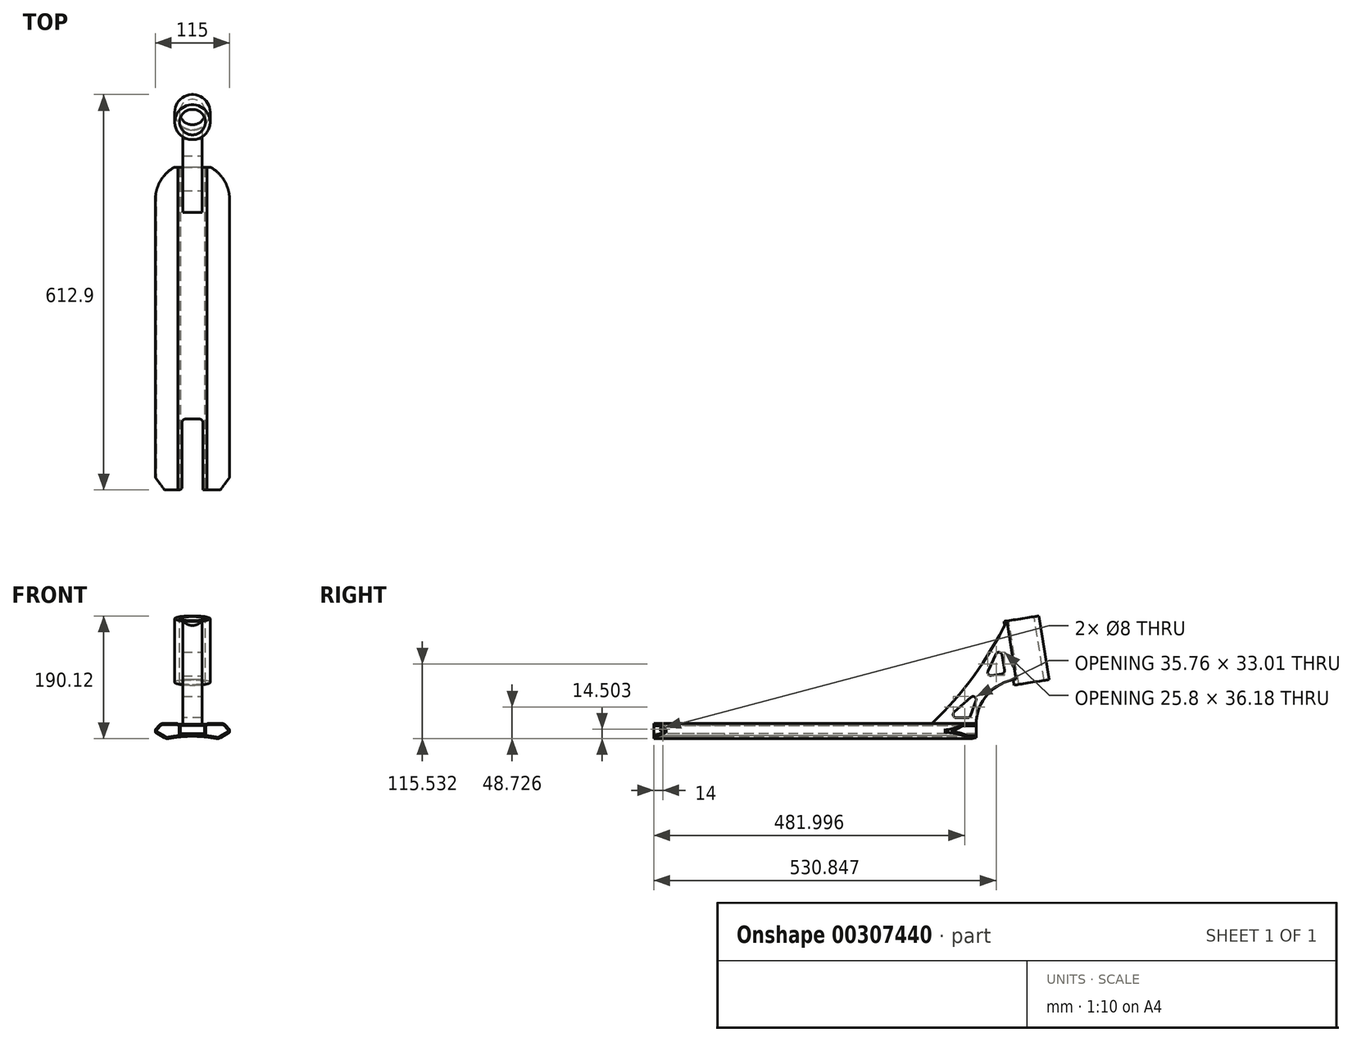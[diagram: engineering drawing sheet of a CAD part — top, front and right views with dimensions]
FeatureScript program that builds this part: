
annotation { "Feature Type Name" : "Feature", "Feature Type Description" : "" }
export const myFeature = defineFeature(function(context is Context, id is Id, definition is map)
    precondition{}
    {
        {
            var Q0;
            Q0=qCreatedBy(makeId("Front.planeOp"),FACE);
            var sketch = newSketch(context, id + "F0", { "sketchPlane" : qUnion([Q0])});
            skLineSegment(sketch, "E0", {"start": v(0, 0) * mm, "end": v(0, 13.62) * mm, "construction": true});
            skLineSegment(sketch, "E1", {"start": v(0, 0) * mm, "end": v(22.5, 0) * mm});
            skLineSegment(sketch, "E2", {"start": v(22.5, 0) * mm, "end": v(22.5, 1.3) * mm});
            skLineSegment(sketch, "E3", {"start": v(22.5, 1.3) * mm, "end": v(49.1, 1.3) * mm});
            skLineSegment(sketch, "E4", {"start": v(57.5, -8.7) * mm, "end": v(49.1, 1.3) * mm});
            skLineSegment(sketch, "E5", {"start": v(57.5, -8.7) * mm, "end": v(57.5, -12.7) * mm});
            skLineSegment(sketch, "E6", {"start": v(57.5, -12.7) * mm, "end": v(40.18, -22.7) * mm});
            skLineSegment(sketch, "E7.MirrorCS", {"start": v(0, 0) * mm, "end": v(-22.5, 0) * mm});
            skLineSegment(sketch, "E8.MirrorCS", {"start": v(-22.5, 0) * mm, "end": v(-22.5, 1.3) * mm});
            skLineSegment(sketch, "E9.MirrorCS", {"start": v(-22.5, 1.3) * mm, "end": v(-49.1, 1.3) * mm});
            skLineSegment(sketch, "E10.MirrorCS", {"start": v(-57.5, -8.7) * mm, "end": v(-49.1, 1.3) * mm});
            skLineSegment(sketch, "E11.MirrorCS", {"start": v(-57.5, -8.7) * mm, "end": v(-57.5, -12.7) * mm});
            skLineSegment(sketch, "E12.MirrorCS", {"start": v(-57.5, -12.7) * mm, "end": v(-40.18, -22.7) * mm});
            skArc(sketch, "E13", {"start": v(40.18, -22.7) * mm, "mid": v(0, -18.62) * mm, "end": v(-40.18, -22.7) * mm});
            skSolve(sketch);
        }
        {
            var Q0;
            Q0 = qSketchRegion(id + "F0", true);
            extrude(context, id + "F1", {"entities" : qUnion([Q0]), "endBound" : BoundingType.SYMMETRIC, "depth" : 500 * mm});
        }
        {
            var Q0;
            Q0=qCreatedBy(makeId("Front.planeOp"),FACE);
            var sketch = newSketch(context, id + "F2", { "sketchPlane" : qUnion([Q0])});
            skLineSegment(sketch, "E14.bottom", {"start": v(19, -14.73) * mm, "end": v(-19, -14.73) * mm});
            skLineSegment(sketch, "E14.top", {"start": v(19, -1.73) * mm, "end": v(-19, -1.73) * mm});
            skLineSegment(sketch, "E14.left", {"start": v(19, -14.73) * mm, "end": v(19, -1.73) * mm});
            skLineSegment(sketch, "E14.right", {"start": v(-19, -14.73) * mm, "end": v(-19, -1.73) * mm});
            skPoint(sketch, "E14.middle", {"position": v(0, -8.23) * mm});
            skSolve(sketch);
        }
        {
            var Q0;
            Q0 = qSketchRegion(id + "F2", true);
            extrude(context, id + "F3", {"entities" : qUnion([Q0]), "operationType" : NewBodyOperationType.REMOVE, "endBound" : BoundingType.SYMMETRIC, "oppositeDirection" : true, "depth" : 500 * mm});
        }
        {
            var Q0;
            Q0=makeQuery(id+"F1.opExtrude","SWEPT_EDGE",EDGE,{"disambiguationData":[OSD([sQuery(id+"F0.wireOp",EDGE,"E2"),sQuery(id+"F0.wireOp",EDGE,"E3")])]});
            var Q1;
            Q1=makeQuery(id+"F1.opExtrude","SWEPT_EDGE",EDGE,{"disambiguationData":[OSD([sQuery(id+"F0.wireOp",EDGE,"E8.MirrorCS"),sQuery(id+"F0.wireOp",EDGE,"E9.MirrorCS")])]});
            fillet(context, id + "F4", {"entities" : qUnion([Q0, Q1]), "radius" : 2 * mm, "tangentPropagation" : true, "allowEdgeOverflow" : false});
        }
        {
            var Q0;
            Q0=makeQuery(id+"F1.opExtrude","SWEPT_EDGE",EDGE,{"disambiguationData":[OSD([sQuery(id+"F0.wireOp",EDGE,"E9.MirrorCS"),sQuery(id+"F0.wireOp",EDGE,"E10.MirrorCS")])]});
            var Q1;
            Q1=makeQuery(id+"F1.opExtrude","SWEPT_EDGE",EDGE,{"disambiguationData":[OSD([sQuery(id+"F0.wireOp",EDGE,"E3"),sQuery(id+"F0.wireOp",EDGE,"E4")])]});
            var Q2;
            Q2=makeQuery(id+"F1.opExtrude","SWEPT_EDGE",EDGE,{"disambiguationData":[OSD([sQuery(id+"F0.wireOp",EDGE,"E6"),sQuery(id+"F0.wireOp",EDGE,"E13")])]});
            var Q3;
            Q3=makeQuery(id+"F1.opExtrude","SWEPT_EDGE",EDGE,{"disambiguationData":[OSD([sQuery(id+"F0.wireOp",EDGE,"E12.MirrorCS"),sQuery(id+"F0.wireOp",EDGE,"E13")])]});
            fillet(context, id + "F5", {"entities" : qUnion([Q0, Q1, Q2, Q3]), "radius" : 9 * mm, "tangentPropagation" : true, "allowEdgeOverflow" : false});
        }
        {
            var Q0;
            Q0=makeQuery(id+"F1.opExtrude","SWEPT_EDGE",EDGE,{"disambiguationData":[OSD([sQuery(id+"F0.wireOp",EDGE,"E10.MirrorCS"),sQuery(id+"F0.wireOp",EDGE,"E11.MirrorCS")])]});
            var Q1;
            Q1=makeQuery(id+"F1.opExtrude","SWEPT_EDGE",EDGE,{"disambiguationData":[OSD([sQuery(id+"F0.wireOp",EDGE,"E11.MirrorCS"),sQuery(id+"F0.wireOp",EDGE,"E12.MirrorCS")])]});
            var Q2;
            Q2=makeQuery(id+"F1.opExtrude","SWEPT_EDGE",EDGE,{"disambiguationData":[OSD([sQuery(id+"F0.wireOp",EDGE,"E4"),sQuery(id+"F0.wireOp",EDGE,"E5")])]});
            var Q3;
            Q3=makeQuery(id+"F1.opExtrude","SWEPT_EDGE",EDGE,{"disambiguationData":[OSD([sQuery(id+"F0.wireOp",EDGE,"E5"),sQuery(id+"F0.wireOp",EDGE,"E6")])]});
            fillet(context, id + "F6", {"entities" : qUnion([Q0, Q1, Q2, Q3]), "radius" : 1 * mm, "tangentPropagation" : true, "allowEdgeOverflow" : false});
        }
        {
            var Q0;
            Q0=makeQuery(id+"F1.opExtrude","CAP_FACE",FACE,{"disambiguationData":[OSD([sQuery(id+"F0.wireOp",EDGE,"E1"),sQuery(id+"F0.wireOp",EDGE,"E2"),sQuery(id+"F0.wireOp",EDGE,"E3"),sQuery(id+"F0.wireOp",EDGE,"E4"),sQuery(id+"F0.wireOp",EDGE,"E5"),sQuery(id+"F0.wireOp",EDGE,"E6"),sQuery(id+"F0.wireOp",EDGE,"E7.MirrorCS"),sQuery(id+"F0.wireOp",EDGE,"E8.MirrorCS"),sQuery(id+"F0.wireOp",EDGE,"E9.MirrorCS"),sQuery(id+"F0.wireOp",EDGE,"E10.MirrorCS"),sQuery(id+"F0.wireOp",EDGE,"E11.MirrorCS"),sQuery(id+"F0.wireOp",EDGE,"E12.MirrorCS"),sQuery(id+"F0.wireOp",EDGE,"E13")])],"isStart":false});
            var sketch = newSketch(context, id + "F7", { "sketchPlane" : qUnion([Q0])});
            skArc(sketch, "E15.0", {"start": v(-20.41, -17.66) * mm, "mid": v(-28.89, -18.7) * mm, "end": v(-37.3, -20.1) * mm});
            skArc(sketch, "E15.1", {"start": v(-42.1, -19.28) * mm, "mid": v(-39.78, -20.12) * mm, "end": v(-37.3, -20.1) * mm});
            skLineSegment(sketch, "E15.2", {"start": v(-24.37, -0.7) * mm, "end": v(-44.91, -0.7) * mm});
            skArc(sketch, "E15.3", {"start": v(-44.91, -0.7) * mm, "mid": v(-47.87, -1.36) * mm, "end": v(-50.27, -3.2) * mm});
            skLineSegment(sketch, "E15.4", {"start": v(-55.93, -9.94) * mm, "end": v(-50.27, -3.2) * mm});
            skLineSegment(sketch, "E15.5", {"start": v(-55.66, -11.45) * mm, "end": v(-42.1, -19.28) * mm});
            skPoint(sketch, "E16.visualSharp", {"position": v(-56.7, -10.85) * mm});
            skArc(sketch, "E16.filletArc", {"start": v(-55.93, -9.94) * mm, "mid": v(-56.15, -10.76) * mm, "end": v(-55.66, -11.45) * mm});
            skArc(sketch, "E17", {"start": v(-24.37, -0.7) * mm, "mid": v(-23.1, -1.15) * mm, "end": v(-22.41, -2.3) * mm});
            skLineSegment(sketch, "E18", {"start": v(-22.41, -2.3) * mm, "end": v(-20.41, -2.3) * mm});
            skLineSegment(sketch, "E19", {"start": v(-20.41, -2.3) * mm, "end": v(-20.41, -17.66) * mm});
            skLineSegment(sketch, "E20", {"start": v(0, 0) * mm, "end": v(0, 11.87) * mm, "construction": true});
            skLineSegment(sketch, "E21.MirrorCS", {"start": v(20.41, -2.3) * mm, "end": v(20.41, -17.66) * mm});
            skLineSegment(sketch, "E22.MirrorCS", {"start": v(22.41, -2.3) * mm, "end": v(20.41, -2.3) * mm});
            skArc(sketch, "E23.MirrorCS", {"start": v(24.37, -0.7) * mm, "mid": v(23.1, -1.15) * mm, "end": v(22.41, -2.3) * mm});
            skLineSegment(sketch, "E24.MirrorCS", {"start": v(24.37, -0.7) * mm, "end": v(44.91, -0.7) * mm});
            skArc(sketch, "E25.MirrorCS", {"start": v(44.91, -0.7) * mm, "mid": v(47.87, -1.36) * mm, "end": v(50.27, -3.2) * mm});
            skLineSegment(sketch, "E26.MirrorCS", {"start": v(55.93, -9.94) * mm, "end": v(50.27, -3.2) * mm});
            skArc(sketch, "E27.MirrorCS", {"start": v(55.93, -9.94) * mm, "mid": v(56.15, -10.76) * mm, "end": v(55.66, -11.45) * mm});
            skLineSegment(sketch, "E28.MirrorCS", {"start": v(55.66, -11.45) * mm, "end": v(42.1, -19.28) * mm});
            skArc(sketch, "E29.MirrorCS", {"start": v(42.1, -19.28) * mm, "mid": v(39.78, -20.12) * mm, "end": v(37.3, -20.1) * mm});
            skArc(sketch, "E30.MirrorCS", {"start": v(20.41, -17.66) * mm, "mid": v(28.89, -18.7) * mm, "end": v(37.3, -20.1) * mm});
            skSolve(sketch);
        }
        {
            var Q0;
            Q0 = qSketchRegion(id + "F7", true);
            extrude(context, id + "F8", {"entities" : qUnion([Q0]), "operationType" : NewBodyOperationType.REMOVE, "endBound" : BoundingType.THROUGH_ALL, "oppositeDirection" : true, "depth" : 25 * mm});
        }
        {
            var Q0;
            Q0=qCreatedBy(makeId("Top.planeOp"),FACE);
            var sketch = newSketch(context, id + "F9", { "sketchPlane" : qUnion([Q0])});
            skArc(sketch, "E31", {"start": v(57.5, 200) * mm, "mid": v(0, 257.5) * mm, "end": v(-57.5, 200) * mm});
            skLineSegment(sketch, "E32", {"start": v(57.5, 200) * mm, "end": v(57.5, 280) * mm});
            skLineSegment(sketch, "E33", {"start": v(57.5, 280) * mm, "end": v(-57.5, 280) * mm});
            skLineSegment(sketch, "E34", {"start": v(-57.5, 280) * mm, "end": v(-57.5, 200) * mm});
            skSolve(sketch);
        }
        {
            var Q0;
            Q0 = qSketchRegion(id + "F9", true);
            extrude(context, id + "F10", {"entities" : qUnion([Q0]), "operationType" : NewBodyOperationType.REMOVE, "endBound" : BoundingType.THROUGH_ALL, "oppositeDirection" : true, "depth" : 25 * mm, "hasSecondDirection" : true, "secondDirectionBound" : SecondDirectionBoundingType.THROUGH_ALL, "secondDirectionOppositeDirection" : false, "secondDirectionDepth" : 25 * mm});
        }
        {
            var Q0;
            Q0=qCreatedBy(makeId("Top.planeOp"),FACE);
            var sketch = newSketch(context, id + "F11", { "sketchPlane" : qUnion([Q0])});
            skLineSegment(sketch, "E35", {"start": v(-16, -140) * mm, "end": v(-16, -250) * mm});
            skLineSegment(sketch, "E36", {"start": v(-16, -250) * mm, "end": v(-43.3, -250) * mm});
            skLineSegment(sketch, "E37", {"start": v(-43.3, -250) * mm, "end": v(-68, -216) * mm});
            skLineSegment(sketch, "E38", {"start": v(-68, -216) * mm, "end": v(-68, -346) * mm});
            skLineSegment(sketch, "E39", {"start": v(-68, -346) * mm, "end": v(68, -346) * mm});
            skLineSegment(sketch, "E40", {"start": v(68, -346) * mm, "end": v(68, -216) * mm});
            skLineSegment(sketch, "E41", {"start": v(16, -140) * mm, "end": v(16, -250) * mm});
            skLineSegment(sketch, "E42", {"start": v(16, -250) * mm, "end": v(43.3, -250) * mm});
            skLineSegment(sketch, "E43", {"start": v(43.3, -250) * mm, "end": v(68, -216) * mm});
            skLineSegment(sketch, "E44", {"start": v(-16, -140) * mm, "end": v(16, -140) * mm});
            skSolve(sketch);
        }
        {
            var Q0;
            Q0 = qSketchRegion(id + "F11", true);
            extrude(context, id + "F12", {"entities" : qUnion([Q0]), "operationType" : NewBodyOperationType.REMOVE, "endBound" : BoundingType.THROUGH_ALL, "oppositeDirection" : true, "depth" : 25 * mm, "hasSecondDirection" : true, "secondDirectionBound" : SecondDirectionBoundingType.THROUGH_ALL, "secondDirectionOppositeDirection" : false, "secondDirectionDepth" : 25 * mm});
        }
        {
            var Q0;
            {var subQ0=sQuery(id+"F11.wireOp",EDGE,"E44");var subQ1=sQuery(id+"F11.wireOp",EDGE,"E35");Q0=makeQuery(id+"F12.boolean.opBoolean","COPY",EDGE,{"disambiguationData":[TD([makeQuery(id+"F1.opExtrude","SWEPT_FACE",FACE,{"disambiguationData":[OSD([sQuery(id+"F0.wireOp",EDGE,"E13")])]})])],"derivedFrom":makeQuery(id+"F12.opExtrude","SWEPT_EDGE",EDGE,{"disambiguationData":[OSD([subQ1,subQ0])]})});}
            var Q1;
            {var subQ0=sQuery(id+"F11.wireOp",EDGE,"E35");var subQ1=sQuery(id+"F11.wireOp",EDGE,"E44");Q1=makeQuery(id+"F12.boolean.opBoolean","COPY",EDGE,{"disambiguationData":[TD([makeQuery(id+"F3.boolean.opBoolean","COPY",FACE,{"derivedFrom":makeQuery(id+"F3.opExtrude","SWEPT_FACE",FACE,{"disambiguationData":[OSD([sQuery(id+"F2.wireOp",EDGE,"E14.top")])]})})])],"derivedFrom":makeQuery(id+"F12.opExtrude","SWEPT_EDGE",EDGE,{"disambiguationData":[OSD([subQ0,subQ1])]})});}
            var Q2;
            {var subQ0=sQuery(id+"F11.wireOp",EDGE,"E41");var subQ1=sQuery(id+"F11.wireOp",EDGE,"E44");Q2=makeQuery(id+"F12.boolean.opBoolean","COPY",EDGE,{"disambiguationData":[TD([makeQuery(id+"F3.boolean.opBoolean","COPY",FACE,{"derivedFrom":makeQuery(id+"F3.opExtrude","SWEPT_FACE",FACE,{"disambiguationData":[OSD([sQuery(id+"F2.wireOp",EDGE,"E14.top")])]})})])],"derivedFrom":makeQuery(id+"F12.opExtrude","SWEPT_EDGE",EDGE,{"disambiguationData":[OSD([subQ0,subQ1])]})});}
            var Q3;
            {var subQ0=sQuery(id+"F11.wireOp",EDGE,"E44");var subQ1=sQuery(id+"F11.wireOp",EDGE,"E41");Q3=makeQuery(id+"F12.boolean.opBoolean","COPY",EDGE,{"disambiguationData":[TD([makeQuery(id+"F1.opExtrude","SWEPT_FACE",FACE,{"disambiguationData":[OSD([sQuery(id+"F0.wireOp",EDGE,"E13")])]})])],"derivedFrom":makeQuery(id+"F12.opExtrude","SWEPT_EDGE",EDGE,{"disambiguationData":[OSD([subQ1,subQ0])]})});}
            var Q4;
            {var subQ2=sQuery(id+"F11.wireOp",EDGE,"E35");Q4=makeQuery(id+"F12.boolean.opBoolean","COPY",EDGE,{"disambiguationData":[TD([makeQuery(id+"F3.boolean.opBoolean","COPY",FACE,{"derivedFrom":makeQuery(id+"F3.opExtrude","SWEPT_FACE",FACE,{"disambiguationData":[OSD([sQuery(id+"F2.wireOp",EDGE,"E14.top")])]})})])],"derivedFrom":makeQuery(id+"F12.opExtrude","SWEPT_EDGE",EDGE,{"disambiguationData":[OSD([subQ2,sQuery(id+"F11.wireOp",EDGE,"E36")])]})});}
            var Q5;
            {var subQ2=sQuery(id+"F11.wireOp",EDGE,"E41");Q5=makeQuery(id+"F12.boolean.opBoolean","COPY",EDGE,{"disambiguationData":[TD([makeQuery(id+"F3.boolean.opBoolean","COPY",FACE,{"derivedFrom":makeQuery(id+"F3.opExtrude","SWEPT_FACE",FACE,{"disambiguationData":[OSD([sQuery(id+"F2.wireOp",EDGE,"E14.top")])]})})])],"derivedFrom":makeQuery(id+"F12.opExtrude","SWEPT_EDGE",EDGE,{"disambiguationData":[OSD([subQ2,sQuery(id+"F11.wireOp",EDGE,"E42")])]})});}
            fillet(context, id + "F13", {"entities" : qUnion([Q0, Q1, Q2, Q3, Q4, Q5]), "radius" : 5 * mm, "tangentPropagation" : true, "allowEdgeOverflow" : false});
        }
        {
            var Q0;
            Q0=qCreatedBy(makeId("Right.planeOp"),FACE);
            var sketch = newSketch(context, id + "F14", { "sketchPlane" : qUnion([Q0])});
            skLineSegment(sketch, "E45", {"start": v(250, 0) * mm, "end": v(180, 0) * mm});
            skLineSegment(sketch, "E46", {"start": v(311.71, 69.5) * mm, "end": v(313.03, 61.23) * mm});
            skLineSegment(sketch, "E47", {"start": v(313.03, 61.23) * mm, "end": v(358.46, 68.43) * mm});
            skLineSegment(sketch, "E48", {"start": v(358.46, 68.43) * mm, "end": v(342.82, 167.2) * mm});
            skLineSegment(sketch, "E49", {"start": v(342.82, 167.2) * mm, "end": v(297.38, 160) * mm});
            skArc(sketch, "E50", {"start": v(180, 0) * mm, "mid": v(245.97, 74.66) * mm, "end": v(297.38, 160) * mm});
            skArc(sketch, "E51", {"start": v(311.71, 69.5) * mm, "mid": v(267.66, 46.48) * mm, "end": v(250, 0) * mm});
            skSolve(sketch);
        }
        {
            var Q0;
            Q0 = qSketchRegion(id + "F14", true);
            extrude(context, id + "F15", {"entities" : qUnion([Q0]), "operationType" : NewBodyOperationType.ADD, "endBound" : BoundingType.SYMMETRIC, "depth" : 30 * mm});
        }
        {
            var Q0;
            Q0=makeQuery(id+"F15.opExtrude","SWEPT_FACE",FACE,{"disambiguationData":[OSD([sQuery(id+"F14.wireOp",EDGE,"E49")])]});
            var sketch = newSketch(context, id + "F16", { "sketchPlane" : qUnion([Q0])});
            skCircle(sketch, "E52", {"center": v(0, 341.75) * mm, "radius": 27.5 * mm});
            skSolve(sketch);
        }
        {
            var Q0;
            Q0 = qSketchRegion(id + "F16", true);
            var Q1;
            Q1=makeQuery(id+"F15.opExtrude","SWEPT_FACE",FACE,{"disambiguationData":[OSD([sQuery(id+"F14.wireOp",EDGE,"E47")])]});
            extrude(context, id + "F17", {"entities" : qUnion([Q0]), "operationType" : NewBodyOperationType.ADD, "endBound" : BoundingType.UP_TO_SURFACE, "oppositeDirection" : true, "endBoundEntityFace" : qUnion([Q1]), "depth" : 25 * mm});
        }
        {
            var Q0;
            Q0=makeQuery(id+"F17.boolean.opBoolean","MERGE",FACE,{"derivedFrom":[makeQuery(id+"F15.opExtrude","SWEPT_FACE",FACE,{"disambiguationData":[OSD([sQuery(id+"F14.wireOp",EDGE,"E49")])]}),makeQuery(id+"F17.opExtrude","CAP_FACE",FACE,{"disambiguationData":[OSD([sQuery(id+"F16.wireOp",EDGE,"E52")])],"isStart":true})]});
            var sketch = newSketch(context, id + "F18", { "sketchPlane" : qUnion([Q0])});
            skPoint(sketch, "E53", {"position": v(0, 341.75) * mm});
            skSolve(sketch);
        }
        {
            var Q0;
            Q0=sQuery(id+"F18.wireOp",VERTEX,"E53");
            var Q1;
            Q1=makeQuery(id+"F1.opExtrude","SWEPT_BODY",BODY,{"disambiguationData":[OSD([sQuery(id+"F0.wireOp",EDGE,"E1"),sQuery(id+"F0.wireOp",EDGE,"E2"),sQuery(id+"F0.wireOp",EDGE,"E3"),sQuery(id+"F0.wireOp",EDGE,"E4"),sQuery(id+"F0.wireOp",EDGE,"E5"),sQuery(id+"F0.wireOp",EDGE,"E6"),sQuery(id+"F0.wireOp",EDGE,"E7.MirrorCS"),sQuery(id+"F0.wireOp",EDGE,"E8.MirrorCS"),sQuery(id+"F0.wireOp",EDGE,"E9.MirrorCS"),sQuery(id+"F0.wireOp",EDGE,"E10.MirrorCS"),sQuery(id+"F0.wireOp",EDGE,"E11.MirrorCS"),sQuery(id+"F0.wireOp",EDGE,"E12.MirrorCS"),sQuery(id+"F0.wireOp",EDGE,"E13")])]});
            hole(context, id + "F19", {"style" : HoleStyle.SIMPLE, "endStyle" : HoleEndStyle.THROUGH, "holeDiameter" : 40 * mm, "isTappedThrough" : true, "tappedDepth" : 12 * mm, "tapClearance" : 3, "locations" : qUnion([Q0]), "scope" : qUnion([Q1])});
        }
        {
            var Q0;
            Q0=makeQuery(id+"F8.boolean.opBoolean","COPY",FACE,{"derivedFrom":makeQuery(id+"F8.opExtrude","SWEPT_FACE",FACE,{"disambiguationData":[OSD([sQuery(id+"F7.wireOp",EDGE,"E21.MirrorCS")])]})});
            var sketch = newSketch(context, id + "F20", { "sketchPlane" : qUnion([Q0])});
            skPoint(sketch, "E54", {"position": v(-236, -7.72) * mm});
            skSolve(sketch);
        }
        {
            var Q0;
            Q0=sQuery(id+"F20.wireOp",VERTEX,"E54");
            var Q1;
            Q1=makeQuery(id+"F1.opExtrude","SWEPT_BODY",BODY,{"disambiguationData":[OSD([sQuery(id+"F0.wireOp",EDGE,"E1"),sQuery(id+"F0.wireOp",EDGE,"E2"),sQuery(id+"F0.wireOp",EDGE,"E3"),sQuery(id+"F0.wireOp",EDGE,"E4"),sQuery(id+"F0.wireOp",EDGE,"E5"),sQuery(id+"F0.wireOp",EDGE,"E6"),sQuery(id+"F0.wireOp",EDGE,"E7.MirrorCS"),sQuery(id+"F0.wireOp",EDGE,"E8.MirrorCS"),sQuery(id+"F0.wireOp",EDGE,"E9.MirrorCS"),sQuery(id+"F0.wireOp",EDGE,"E10.MirrorCS"),sQuery(id+"F0.wireOp",EDGE,"E11.MirrorCS"),sQuery(id+"F0.wireOp",EDGE,"E12.MirrorCS"),sQuery(id+"F0.wireOp",EDGE,"E13")])]});
            hole(context, id + "F21", {"style" : HoleStyle.SIMPLE, "endStyle" : HoleEndStyle.BLIND, "holeDiameter" : 8 * mm, "holeDepth" : 50 * mm, "isTappedThrough" : true, "tappedDepth" : 12 * mm, "tapClearance" : 3, "locations" : qUnion([Q0]), "scope" : qUnion([Q1])});
        }
        {
            var Q0;
            Q0=makeQuery(id+"F15.opExtrude","CAP_FACE",FACE,{"disambiguationData":[OSD([sQuery(id+"F14.wireOp",EDGE,"E45"),sQuery(id+"F14.wireOp",EDGE,"E46"),sQuery(id+"F14.wireOp",EDGE,"E47"),sQuery(id+"F14.wireOp",EDGE,"E48"),sQuery(id+"F14.wireOp",EDGE,"E49"),sQuery(id+"F14.wireOp",EDGE,"E50"),sQuery(id+"F14.wireOp",EDGE,"E51")])],"isStart":false});
            var sketch = newSketch(context, id + "F22", { "sketchPlane" : qUnion([Q0])});
            skLineSegment(sketch, "E55", {"start": v(256.38, 55) * mm, "end": v(240, 10) * mm});
            skLineSegment(sketch, "E56", {"start": v(240, 10) * mm, "end": v(206, 10) * mm});
            skLineSegment(sketch, "E57", {"start": v(206, 10) * mm, "end": v(256.38, 55) * mm});
            skLineSegment(sketch, "E58", {"start": v(264.47, 73.8) * mm, "end": v(294.47, 78.54) * mm});
            skLineSegment(sketch, "E59", {"start": v(294.47, 78.54) * mm, "end": v(287.34, 123.54) * mm});
            skLineSegment(sketch, "E60", {"start": v(287.34, 123.54) * mm, "end": v(264.47, 73.8) * mm});
            skSolve(sketch);
        }
        {
            var Q0;
            Q0 = qSketchRegion(id + "F22", true);
            extrude(context, id + "F23", {"entities" : qUnion([Q0]), "operationType" : NewBodyOperationType.REMOVE, "endBound" : BoundingType.THROUGH_ALL, "depth" : 25 * mm, "hasSecondDirection" : true, "secondDirectionBound" : SecondDirectionBoundingType.THROUGH_ALL, "secondDirectionOppositeDirection" : true, "secondDirectionDepth" : 25 * mm});
        }
        {
            var Q0;
            Q0=makeQuery(id+"F23.boolean.opBoolean","COPY",EDGE,{"derivedFrom":makeQuery(id+"F23.opExtrude","SWEPT_EDGE",EDGE,{"disambiguationData":[OSD([sQuery(id+"F22.wireOp",EDGE,"E58"),sQuery(id+"F22.wireOp",EDGE,"E59")])]})});
            var Q1;
            Q1=makeQuery(id+"F23.boolean.opBoolean","COPY",EDGE,{"derivedFrom":makeQuery(id+"F23.opExtrude","SWEPT_EDGE",EDGE,{"disambiguationData":[OSD([sQuery(id+"F22.wireOp",EDGE,"E55"),sQuery(id+"F22.wireOp",EDGE,"E56")])]})});
            var Q2;
            Q2=makeQuery(id+"F23.boolean.opBoolean","COPY",EDGE,{"derivedFrom":makeQuery(id+"F23.opExtrude","SWEPT_EDGE",EDGE,{"disambiguationData":[OSD([sQuery(id+"F22.wireOp",EDGE,"E55"),sQuery(id+"F22.wireOp",EDGE,"E57")])]})});
            var Q3;
            Q3=makeQuery(id+"F23.boolean.opBoolean","COPY",EDGE,{"derivedFrom":makeQuery(id+"F23.opExtrude","SWEPT_EDGE",EDGE,{"disambiguationData":[OSD([sQuery(id+"F22.wireOp",EDGE,"E59"),sQuery(id+"F22.wireOp",EDGE,"E60")])]})});
            var Q4;
            Q4=makeQuery(id+"F23.boolean.opBoolean","COPY",EDGE,{"derivedFrom":makeQuery(id+"F23.opExtrude","SWEPT_EDGE",EDGE,{"disambiguationData":[OSD([sQuery(id+"F22.wireOp",EDGE,"E56"),sQuery(id+"F22.wireOp",EDGE,"E57")])]})});
            var Q5;
            Q5=makeQuery(id+"F23.boolean.opBoolean","COPY",EDGE,{"derivedFrom":makeQuery(id+"F23.opExtrude","SWEPT_EDGE",EDGE,{"disambiguationData":[OSD([sQuery(id+"F22.wireOp",EDGE,"E58"),sQuery(id+"F22.wireOp",EDGE,"E60")])]})});
            fillet(context, id + "F24", {"entities" : qUnion([Q0, Q1, Q2, Q3, Q4, Q5]), "radius" : 5 * mm, "tangentPropagation" : true, "allowEdgeOverflow" : false});
        }
    });
